# Revit family: IS_Retta_B8986_BIM_DE
name_source: partatom
category: Plumbing Fixtures
revit_build: Autodesk Revit MEP 2016 (Build: 20161004_0715(x64)
units: mm (PartAtom-declared; Revit-internal decimal feet)

## family parameters
Always vertical = No
Cut with Voids When Loaded = No
OmniClass Number = 23.45.55.17
OmniClass Title = Mixing Faucets
Part Type = Normal
Room Calculation Point = No
Round Connector Dimension = Use Diameter
Shared = No
Work Plane-Based = No

## types (2) — shared parameters
Accessories = www.idealstandard.de\ersatzteile
AssetType = Fixed
BIMobject category = Taps & Mixers
BOSUseNativeGeometries = 1
Brand = Ideal Standard
Brand url = http://www.idealstandard.de
ConnectionType = Plumbing
CurrencyUnit = €
CurrentRevision = 1
Date of publishing = 20/12/2017
DurationUnit = Year
Edition number = 1
IFC Classification = Sanitary Terminal
IfcExportAs = IfcSanitaryTerminalType
Installation instructions = http://www.idealstandard.de
InstallationInstructions = www.idealstandard.de\produkte
MaintenanceInformation = www.idealstandard.de\produkte
Manufacturer name = Ideal Standard
ManufacturerURL = http://www.idealstandard.de
Material main = Brass
NBS Reference Code = 35-79-79
NBS Reference Description = Sink Water Supply Fittings
NettWeight = 2.67 Kg
NominalDepth = 236 mm
NominalHeight = 330 mm
NominalLength = 236 mm
NominalWidth = 115 mm
OmniClass Code = 23-31 11 00
OmniClass Description = Faucets
Product Guid = 4c7b5743-bdcc-4f6f-b3ac-c37232ba665a
Product SKU = B8986
Product data url = https://bimobject.com
Product family = Sanitary
Product group = Kitchen Mixer
Product name = RETTA kitchen mixer one hole high spout single lever hand, low pressure
Product url = http://www.idealstandard.de
ProductInformation = www.idealstandard.de/produkte
QR code = http://bimobject.com
Size = 330 x 236 x 115mm
Space = Internal
SpareParts = www.idealstandard.de/ersatzteile
Technical description = http://www.idealstandard.de
TestPressure = 10 Bar
URL = http://www.idealstandard.de
Uniclass 1.4 Code = L8212
Uniclass 1.4 Description = Fittings
Uniclass 2.0 Code = PR-35-79-79
Uniclass 2.0 Description = Sink Water Supply Fittings
Uniclass 2015 Code = Pr_40_20_87_82
Uniclass 2015 Name = Sink manual water supply sets
Uniclass2015Code = Pr_40_20_87_82
Uniclass2015Title = Sink manual water supply sets
Uniclass2015Version = Products v1.1
Version = 1
VolumeUnits = Litres
Weight Net (Kg) = 2.67
zero-valued in all types: Cost, InletConnectionSize, Nominal height, Nominal width

## per-type parameters (varying)
| type | BIMObjectName | BarCode | CodePerformance | Color | Description | EAN code | ExpectedLife | Features | Finish | MainColor | Material | Model | ModelNumber | ModelReference | Name | Shape |
| B8986AA - RETTA kitchen mixer one hole high spout single lever hand, low pressure | ISI_IdealStandard_SinkManualWaterSupplySets_Retta_B8986AA | 3800861016915 | 0 | Chrome | IS Küchenarm. RETTA ND m.hohem Auslauf Ausladung 192mm Chrom | https://3800861016915 | 25 | IS Küchenarm. RETTA ND m.hohem Auslauf Ausladung 192mm Chrom | Chrome | Chrome | Brass | B8986AA | B8986AA | IS Küchenarm. RETTA ND m.hohem Auslauf Ausladung 192mm Chrom | SinkManualWaterSupplySets_Retta_B8986AA | Sculptured |
| B8986GN - RETTA kitchen mixer one hole high spout single lever hand, low pressure | ISI_IdealStandard_SinkManualWaterSupplySets_Retta_B8986GN | 3800861039013 |  |  |  | https://3800861039013 |  |  |  |  |  | B8986GN | B8986GN |  | SinkManualWaterSupplySets_Retta_B8986GN |  |

## geometry (parser evidence)
native form markers: Blend x4, Sweep x2
no freeform markers — native parametric forms only
